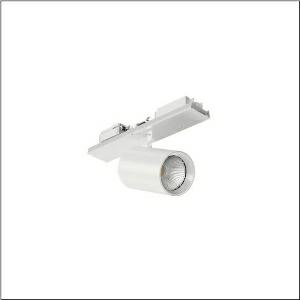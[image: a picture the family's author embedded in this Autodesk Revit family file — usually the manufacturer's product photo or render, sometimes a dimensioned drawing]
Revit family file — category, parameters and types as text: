
# Revit family: licross_r__spot_31_51sl12da43b_285d
name_source: partatom
category: Lighting Fixtures
units: mm (PartAtom-declared; Revit-internal decimal feet)

## family parameters
Cut with Voids When Loaded = No
Host = Face
Light Source = No
Part Type = Normal
Room Calculation Point = No
Round Connector Dimension = Use Diameter
Shared = No

## types (1)
- --- (1 x LED, 3650 lm, 28.6 W, 4000K)
    Apparent Load = 29 VA
    CIE Flux Codes = 93 97 99 100 100
    Color Rendering = 90
    Color Temperature = 4000K
    Default Elevation = 1800 mm
    Description = Licross® Spot 31, directional spotlight, light control with lens, of plastic, LED rated luminous flux: 3.650lm, light colour: 940, with plug, 5-pole, mains connection: 220..240V, AC, 50/60Hz, of aluminium, traffic white (RAL 9016), length: 300mm, diameter: 90mm, protection rating (complete): IP20, insulation class (complete): insulation class I (protective earthing), certification: CE, packaging unit: 1 piece
    Height = 175 mm
    Lamp = 1 x LED
    Lamp Light Flux = 3650 lm
    Lamp Power = 28.6 W
    Lamp count = 1
    Length = 90 mm
    Luminous efficacy = 128 lm/W
    Manufacturer = Siteco
    ModVariant = No
    Model = 51SL12DA43B
    Mounting Place = Ceiling
    Mounting Type = Pendant
    Number of Poles = 1
    OnlyDefault = Yes
    Power Factor = 1
    Product Name = Licross® Spot 31
    Product group = directional spotlight
    ProductGroupID = 906
    Protection Class = Protection class I
    Protection Degree = IP 20
    RLX_Detail_Level = 1
    RLX_Emergency_Light_Flux = 0 lm
    RLX_Emergency_Type = 0
    RLX_Emergency_Type_DB = No
    RlxData = <blob elided: 14789 chars, md5=5d334b34>
    Socket = socket
    Standby Power = 0 W
    System Light Flux = 3650 lm
    System Power = 29 W
    Type Comments = factory setting: luminous flux: 100 % | (ON | ON | ON) | 700 mA
    Type Image = l_1245720.jpg
    URL = http://relux.com
    VarID = @adj_132616
    Voltage = 0 V
    Weight = 0.00 kg
    Width = 0 mm  [stored 0 ft]

note: [stored X ft] marks values corroborated as IEEE doubles in the binary element streams (Revit-internal decimal feet)

## geometry (parser evidence)
native form markers: Sweep x11
no freeform markers — native parametric forms only
